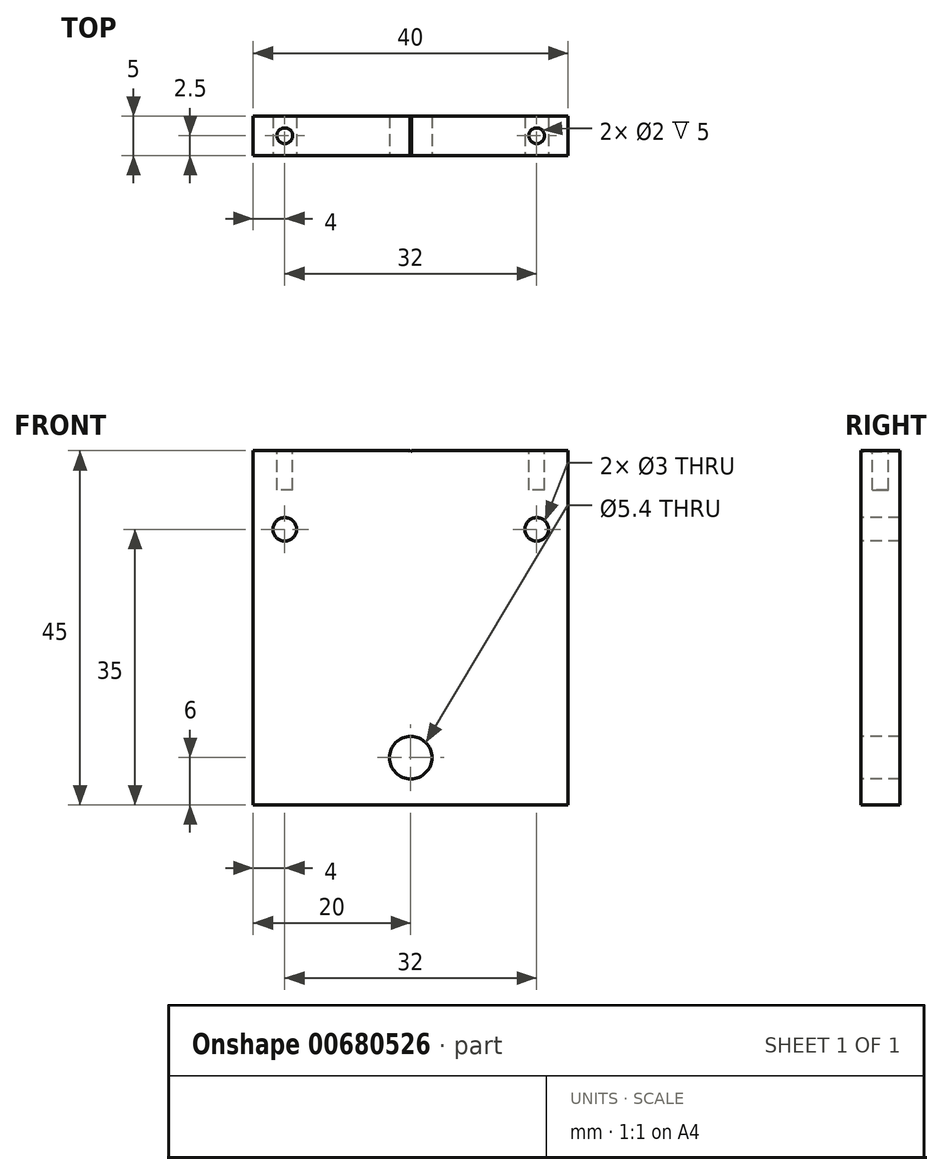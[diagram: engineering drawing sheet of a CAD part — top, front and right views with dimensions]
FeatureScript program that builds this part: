
annotation { "Feature Type Name" : "Feature", "Feature Type Description" : "" }
export const myFeature = defineFeature(function(context is Context, id is Id, definition is map)
    precondition{}
    {
        {
            var Q0;
            Q0=qCreatedBy(makeId("Front.planeOp"),FACE);
            var sketch = newSketch(context, id + "F0", { "sketchPlane" : qUnion([Q0])});
            skLineSegment(sketch, "E0.bottom", {"start": v(-20, 22.5) * mm, "end": v(20, 22.5) * mm});
            skLineSegment(sketch, "E0.top", {"start": v(-20, -22.5) * mm, "end": v(20, -22.5) * mm});
            skLineSegment(sketch, "E0.left", {"start": v(-20, 22.5) * mm, "end": v(-20, -22.5) * mm});
            skLineSegment(sketch, "E0.right", {"start": v(20, 22.5) * mm, "end": v(20, -22.5) * mm});
            skPoint(sketch, "E0.middle", {"position": v(0, 0) * mm});
            skSolve(sketch);
        }
        {
            var Q0;
            Q0=makeQuery(id+"F0.imprint","IMPRINT",FACE,{"disambiguationData":[TD([[makeQuery(id+"F0.imprint","IMPRINT",EDGE,{"derivedFrom":sQuery(id+"F0.wireOp",EDGE,"E0.bottom")}),-1.0]])]});
            extrude(context, id + "F1", {"entities" : qUnion([Q0]), "depth" : 5 * mm, "offsetDistance" : 25 * mm});
        }
        {
            var Q0;
            Q0=makeQuery(id+"F1.opExtrude","CAP_FACE",FACE,{"disambiguationData":[OSD([sQuery(id+"F0.wireOp",EDGE,"E0.bottom"),sQuery(id+"F0.wireOp",EDGE,"E0.top"),sQuery(id+"F0.wireOp",EDGE,"E0.left"),sQuery(id+"F0.wireOp",EDGE,"E0.right")])],"isStart":false});
            var sketch = newSketch(context, id + "F2", { "sketchPlane" : qUnion([Q0])});
            skCircle(sketch, "E1", {"center": v(16, 12.5) * mm, "radius": 1.5 * mm});
            skCircle(sketch, "E2", {"center": v(-16, 12.5) * mm, "radius": 1.5 * mm});
            skSolve(sketch);
        }
        {
            var Q0;
            Q0 = qSketchRegion(id + "F2", true);
            extrude(context, id + "F3", {"entities" : qUnion([Q0]), "operationType" : NewBodyOperationType.REMOVE, "oppositeDirection" : true, "depth" : 25 * mm, "offsetDistance" : 25 * mm});
        }
        {
            var Q0;
            {var subQ1=sQuery(id+"F0.wireOp",EDGE,"E0.left");var subQ3=sQuery(id+"F0.wireOp",EDGE,"E0.bottom");Q0=makeQuery(id+"FwaKjzzbafGnsFd_1.boolean.opBoolean","SPLIT",FACE,{"disambiguationData":[TD([makeQuery(id+"F1.opExtrude","SWEPT_FACE",FACE,{"disambiguationData":[OSD([subQ1])]})])],"derivedFrom":makeQuery(id+"F1.opExtrude","SWEPT_FACE",FACE,{"disambiguationData":[OSD([subQ3])]})});}
            var sketch = newSketch(context, id + "F4", { "sketchPlane" : qUnion([Q0])});
            skPoint(sketch, "E3.centerSnap0", {"position": v(-20, -2.5) * mm});
            skPoint(sketch, "E4", {"position": v(-16, -2.5) * mm});
            skPoint(sketch, "E5", {"position": v(16, -2.5) * mm});
            skSolve(sketch);
        }
        {
            var Q0;
            Q0=makeQuery(id+"F1.opExtrude","CAP_FACE",FACE,{"disambiguationData":[OSD([sQuery(id+"F0.wireOp",EDGE,"E0.bottom"),sQuery(id+"F0.wireOp",EDGE,"E0.top"),sQuery(id+"F0.wireOp",EDGE,"E0.left"),sQuery(id+"F0.wireOp",EDGE,"E0.right")])],"isStart":false});
            var sketch = newSketch(context, id + "F5", { "sketchPlane" : qUnion([Q0])});
            skCircle(sketch, "E6.cCircle", {"center": v(0, 22.5) * mm, "radius": 0.1 * mm, "construction": true});
            skLineSegment(sketch, "E6.0", {"start": v(-0.17, 22.6) * mm, "end": v(0.17, 22.6) * mm});
            skLineSegment(sketch, "E6.1", {"start": v(0.17, 22.6) * mm, "end": v(0, 22.3) * mm});
            skLineSegment(sketch, "E6.2", {"start": v(0, 22.3) * mm, "end": v(-0.17, 22.6) * mm});
            skPoint(sketch, "E6.0.midPoint", {"position": v(0, 22.6) * mm});
            skSolve(sketch);
        }
        {
            var Q0;
            Q0 = qSketchRegion(id + "F5", true);
            extrude(context, id + "F6", {"entities" : qUnion([Q0]), "operationType" : NewBodyOperationType.REMOVE, "oppositeDirection" : true, "depth" : 25 * mm, "offsetDistance" : 25 * mm});
        }
        {
            var Q0;
            {var subQ0=sQuery(id+"F0.wireOp",EDGE,"E0.bottom");Q0=makeQuery(id+"F4.imprint","IMPRINT",FACE,{"disambiguationData":[TD([[makeQuery(id+"F4.imprint","IMPRINT",EDGE,{"derivedFrom":makeQuery(id+"F1.opExtrude","CAP_EDGE",EDGE,{"disambiguationData":[OSD([subQ0])],"isStart":true})}),-1.0]])]});}
            var sketch = newSketch(context, id + "F7", { "sketchPlane" : qUnion([Q0])});
            skCircle(sketch, "E7", {"center": v(16, -2.5) * mm, "radius": 1 * mm});
            skCircle(sketch, "E8", {"center": v(-16, -2.5) * mm, "radius": 1 * mm});
            skSolve(sketch);
        }
        {
            var Q0;
            Q0 = qSketchRegion(id + "F7", true);
            extrude(context, id + "F8", {"entities" : qUnion([Q0]), "operationType" : NewBodyOperationType.REMOVE, "oppositeDirection" : true, "depth" : 5 * mm, "offsetDistance" : 25 * mm});
        }
        {
            var Q0;
            Q0=makeQuery(id+"F1.opExtrude","CAP_FACE",FACE,{"disambiguationData":[OSD([sQuery(id+"F0.wireOp",EDGE,"E0.bottom"),sQuery(id+"F0.wireOp",EDGE,"E0.top"),sQuery(id+"F0.wireOp",EDGE,"E0.left"),sQuery(id+"F0.wireOp",EDGE,"E0.right")])],"isStart":false});
            var sketch = newSketch(context, id + "F9", { "sketchPlane" : qUnion([Q0])});
            skCircle(sketch, "E9", {"center": v(0, -16.5) * mm, "radius": 2.7 * mm});
            skSolve(sketch);
        }
        {
            var Q0;
            Q0 = qSketchRegion(id + "F9", true);
            extrude(context, id + "F10", {"entities" : qUnion([Q0]), "operationType" : NewBodyOperationType.REMOVE, "oppositeDirection" : true, "depth" : 25 * mm, "offsetDistance" : 25 * mm});
        }
    });
